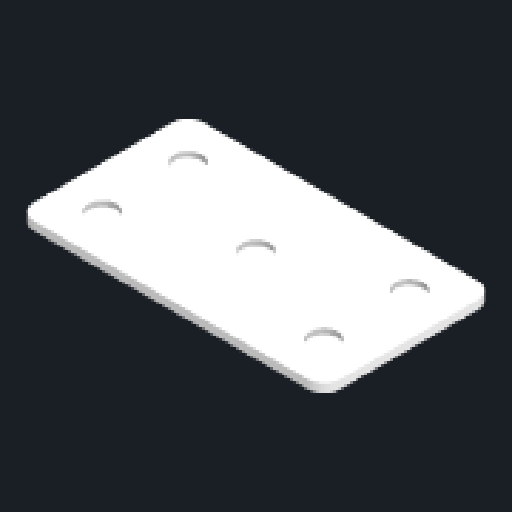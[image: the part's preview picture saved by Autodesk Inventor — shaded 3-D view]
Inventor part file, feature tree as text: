
AUTODESK INVENTOR PART (.ipt)
format: ipt  version: 2025 (Build 290162000, 162)  size: 145,920 bytes
history: native  units: in
note: dims shown in document units (in); Inventor stores cm internally (conversion verified against a paired STEP export)
features: extrude x1, sketch x1, projected_geometry x1
ambient origin geometry x8: Origin, YZ Plane, XZ Plane, XY Plane, X Axis, Y Axis, Z Axis, Center Point
bodies: Solid1 (feature_tree), Body1 (feature_tree)
feature tree (3):
  extrude  "Extrusion2"  Depth=0.0787in
  sketch  "Sketch2"  dims[d2=0.007in d3=0.007in d4=0.007in d5=0.007in d6=0.007in d7=0.0787in d8=0.0in]
  projected_geometry  "Projected Loop2"
